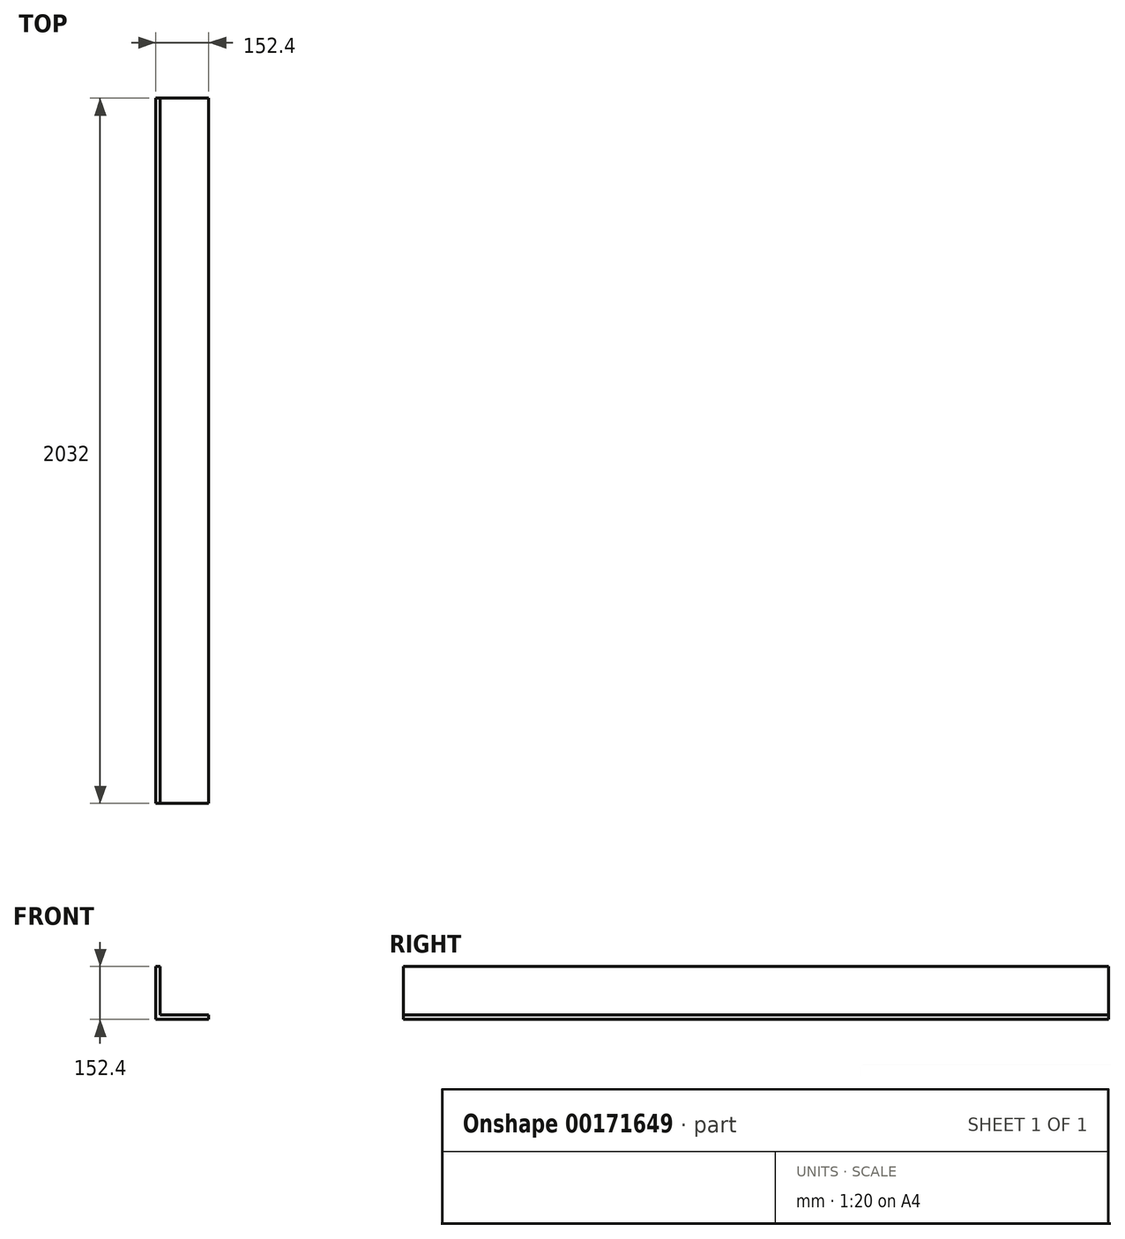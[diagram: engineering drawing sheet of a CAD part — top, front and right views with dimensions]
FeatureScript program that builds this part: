
annotation { "Feature Type Name" : "Feature", "Feature Type Description" : "" }
export const myFeature = defineFeature(function(context is Context, id is Id, definition is map)
    precondition{}
    {
        {
            var Q0;
            Q0=qCreatedBy(makeId("Front.planeOp"),FACE);
            var sketch = newSketch(context, id + "F0", { "sketchPlane" : qUnion([Q0])});
            skLineSegment(sketch, "E0.bottom", {"start": v(-6.35, 152.4) * mm, "end": v(6.35, 152.4) * mm});
            skLineSegment(sketch, "E0.top", {"start": v(-6.35, 0) * mm, "end": v(6.35, 0) * mm});
            skLineSegment(sketch, "E0.left", {"start": v(-6.35, 152.4) * mm, "end": v(-6.35, 0) * mm});
            skLineSegment(sketch, "E0.right", {"start": v(6.35, 152.4) * mm, "end": v(6.35, 12.7) * mm});
            skLineSegment(sketch, "E1.bottom", {"start": v(0, 0) * mm, "end": v(146.05, 0) * mm});
            skLineSegment(sketch, "E1.top", {"start": v(6.35, 12.7) * mm, "end": v(146.05, 12.7) * mm});
            skLineSegment(sketch, "E1.right", {"start": v(146.05, 0) * mm, "end": v(146.05, 12.7) * mm});
            skSolve(sketch);
        }
        {
            var Q0;
            Q0=makeQuery(id+"F0.imprint","IMPRINT",FACE,{"disambiguationData":[TD([[makeQuery(id+"F0.imprint","IMPRINT",EDGE,{"derivedFrom":sQuery(id+"F0.wireOp",EDGE,"E0.bottom")}),-1.0]])]});
            extrude(context, id + "F1", {"entities" : qUnion([Q0]), "depth" : 2032 * mm});
        }
    });
